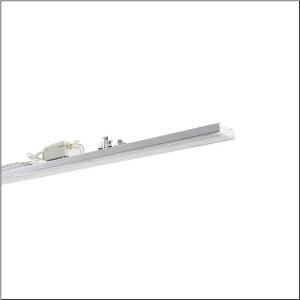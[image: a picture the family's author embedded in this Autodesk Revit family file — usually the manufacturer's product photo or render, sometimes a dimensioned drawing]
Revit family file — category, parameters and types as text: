
# Revit family: licross_r__21_recessed_ho_52tl18dv4l2m_8c23
name_source: partatom
category: Lighting Fixtures
units: mm (PartAtom-declared; Revit-internal decimal feet)

## family parameters
Cut with Voids When Loaded = No
Host = Face
Light Source = No
Part Type = Normal
Room Calculation Point = No
Round Connector Dimension = Use Diameter
Shared = No

## types (1)
- --- (1 x LED, 22480 lm, 125.6 W, 4000K)
    Apparent Load = 126 VA
    CIE Flux Codes = 75 94 99 100 100
    Color Rendering = 80
    Color Temperature = 4000K
    Default Elevation = 1800 mm
    Description = Licross® 21 Recessed HO, luminaire insert, of sheet steel, galvanised, coil coated, white, length: 2.250mm, width: 66mm, height: 67mm, LED rated luminous flux: 22.480lm, light colour: 840, control gear: DALI 2, with plug, 5-pole, with phase selection, mains connection: 220..240V, AC, 50/60Hz, rated input power: 126W, halogen-free wiring, primary light control with lens, of plastic, primary optical cover: cover, of PMMA, light emission: direct distribution, primary light characteristic: symmetric, protection rating (complete): IP40, insulation class (complete): insulation class I (protective earthing), certification: CE, ENEC, VDE, UKCA, protection symbol: D if used in an environment without relevant dust loads with corresponding accessories, impact resistance: IK06, permissible ambient temperature for indoor applications: -40..+30°C, corresponds to IFS (International Featured Standards) requirements for safety and quality in the food industry, reducing of maximum allowable ambient temperature of 5°C with ceiling mounting, LABS conformity tested according to VDMA 24364:2018-05, packaging unit: 1 piece
    Height = 58 mm
    Lamp = 1 x LED
    Lamp Light Flux = 22480 lm
    Lamp Power = 125.6 W
    Lamp count = 1
    Length = 2250 mm
    Luminous efficacy = 179 lm/W
    Manufacturer = Siteco
    ModVariant = No
    Model = 52TL18DV4L2M
    Mounting Place = Ceiling
    Mounting Type = Pendant
    Number of Poles = 1
    OnlyDefault = Yes
    Power Factor = 1
    Product Name = Licross® 21 Recessed HO
    Product group = luminaire insert
    ProductGroupID = 901
    Protection Class = Protection class I
    Protection Degree = IP 40
    RLX_Detail_Level = 1
    RLX_Emergency_Light_Flux = 0 lm
    RLX_Emergency_Type = 0
    RLX_Emergency_Type_DB = No
    RlxData = <blob elided: 29761 chars, md5=bdef850d>
    Socket = socket
    Standby Power = 0 W
    System Light Flux = 22480 lm
    System Power = 126 W
    Type Comments = factory setting: luminous flux: 100 % | dim-lin: 254 | 489 mA
    Type Image = l_1296930.jpg
    URL = http://relux.com
    VarID = @adj_057371
    Voltage = 0 V
    Weight = 0.00 kg
    Width = 66 mm

## geometry (parser evidence)
native form markers: Blend x4, Sweep x11
no freeform markers — native parametric forms only
